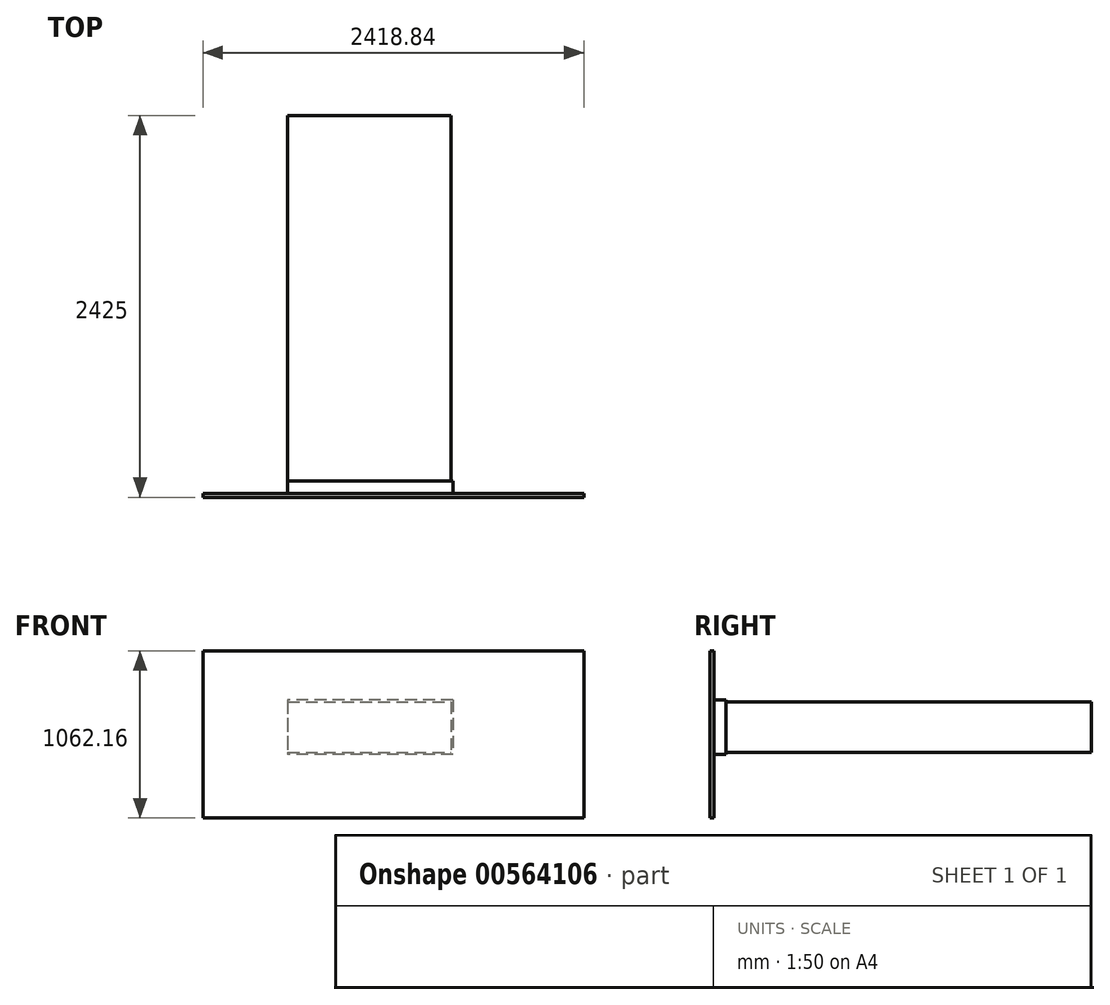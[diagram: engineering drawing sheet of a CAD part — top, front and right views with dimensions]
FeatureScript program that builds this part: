
annotation { "Feature Type Name" : "Feature", "Feature Type Description" : "" }
export const myFeature = defineFeature(function(context is Context, id is Id, definition is map)
    precondition{}
    {
        {
            var Q0;
            Q0=qCreatedBy(makeId("Top.planeOp"),FACE);
            var sketch = newSketch(context, id + "F0", { "sketchPlane" : qUnion([Q0])});
            skLineSegment(sketch, "E0", {"start": v(-707.95, 1209.86) * mm, "end": v(329.05, 1209.86) * mm});
            skLineSegment(sketch, "E1", {"start": v(329.05, 1209.86) * mm, "end": v(329.05, -1112.14) * mm});
            skLineSegment(sketch, "E2", {"start": v(329.05, -1112.14) * mm, "end": v(342.05, -1112.14) * mm});
            skLineSegment(sketch, "E3", {"start": v(342.05, -1112.14) * mm, "end": v(342.05, -1190.14) * mm});
            skLineSegment(sketch, "E4", {"start": v(342.05, -1190.14) * mm, "end": v(-707.95, -1190.14) * mm});
            skLineSegment(sketch, "E5", {"start": v(-707.95, -1190.14) * mm, "end": v(-707.95, 1209.86) * mm});
            skSolve(sketch);
        }
        {
            var Q0;
            Q0=makeQuery(id+"F0.imprint","IMPRINT",FACE,{"disambiguationData":[TD([[makeQuery(id+"F0.imprint","IMPRINT",EDGE,{"derivedFrom":sQuery(id+"F0.wireOp",EDGE,"E0")}),-1.0]])]});
            extrude(context, id + "F1", {"entities" : qUnion([Q0]), "depth" : 320 * mm, "offsetDistance" : 25 * mm});
        }
        {
            var Q0;
            Q0=makeQuery(id+"F1.opExtrude","SWEPT_FACE",FACE,{"disambiguationData":[OSD([sQuery(id+"F0.wireOp",EDGE,"E5")])]});
            var sketch = newSketch(context, id + "F2", { "sketchPlane" : qUnion([Q0])});
            skLineSegment(sketch, "E6.bottom", {"start": v(1190.14, 333) * mm, "end": v(1112.14, 333) * mm});
            skLineSegment(sketch, "E6.top", {"start": v(1190.14, -13) * mm, "end": v(1112.14, -13) * mm});
            skLineSegment(sketch, "E6.left", {"start": v(1190.14, 333) * mm, "end": v(1190.14, -13) * mm});
            skLineSegment(sketch, "E6.right", {"start": v(1112.14, 333) * mm, "end": v(1112.14, -13) * mm});
            skSolve(sketch);
        }
        {
            var Q0;
            Q0 = qSketchRegion(id + "F2", true);
            var Q1;
            Q1=makeQuery(id+"F1.opExtrude","SWEPT_FACE",FACE,{"disambiguationData":[OSD([sQuery(id+"F0.wireOp",EDGE,"E3")])]});
            extrude(context, id + "F3", {"entities" : qUnion([Q0]), "operationType" : NewBodyOperationType.ADD, "endBound" : BoundingType.UP_TO_SURFACE, "oppositeDirection" : true, "depth" : 25 * mm, "endBoundEntityFace" : qUnion([Q1]), "offsetDistance" : 25 * mm});
        }
        {
            var Q0;
            Q0=makeQuery(id+"F3.boolean.opBoolean","MERGE",FACE,{"derivedFrom":[makeQuery(id+"F1.opExtrude","SWEPT_FACE",FACE,{"disambiguationData":[OSD([sQuery(id+"F0.wireOp",EDGE,"E4")])]}),makeQuery(id+"F3.opExtrude","SWEPT_FACE",FACE,{"disambiguationData":[OSD([sQuery(id+"F2.wireOp",EDGE,"E6.left")])]})]});
            var sketch = newSketch(context, id + "F4", { "sketchPlane" : qUnion([Q0])});
            skLineSegment(sketch, "E7.bottom", {"start": v(-1246.02, 645.19) * mm, "end": v(1172.82, 645.19) * mm});
            skLineSegment(sketch, "E7.top", {"start": v(-1246.02, -416.97) * mm, "end": v(1172.82, -416.97) * mm});
            skLineSegment(sketch, "E7.left", {"start": v(-1246.02, 645.19) * mm, "end": v(-1246.02, -416.97) * mm});
            skLineSegment(sketch, "E7.right", {"start": v(1172.82, 645.19) * mm, "end": v(1172.82, -416.97) * mm});
            skSolve(sketch);
        }
        {
            var Q0;
            {var subQ0=sQuery(id+"F2.wireOp",EDGE,"E6.left");var subQ1=sQuery(id+"F2.wireOp",EDGE,"E6.bottom");Q0=makeQuery(id+"F4.imprint","IMPRINT",FACE,{"disambiguationData":[TD([[makeQuery(id+"F4.imprint","IMPRINT",EDGE,{"derivedFrom":makeQuery(id+"F3.opExtrude","SWEPT_EDGE",EDGE,{"disambiguationData":[OSD([subQ1,subQ0])]})}),1.0]])]});}
            var Q1;
            Q1=makeQuery(id+"F4.imprint","IMPRINT",FACE,{"disambiguationData":[TD([[makeQuery(id+"F4.imprint","IMPRINT",EDGE,{"derivedFrom":sQuery(id+"F4.wireOp",EDGE,"E7.bottom")}),-1.0]])]});
            extrude(context, id + "F5", {"entities" : qUnion([Q0, Q1]), "operationType" : NewBodyOperationType.ADD, "depth" : 25 * mm, "offsetDistance" : 25 * mm});
        }
    });
